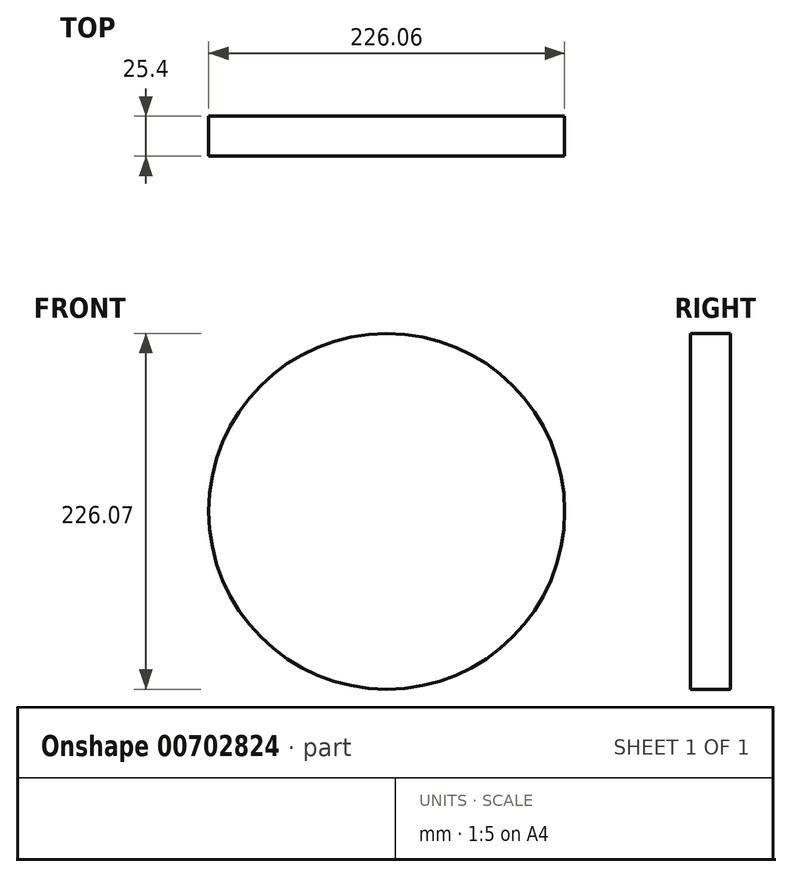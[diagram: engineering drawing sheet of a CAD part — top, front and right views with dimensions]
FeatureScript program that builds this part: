
annotation { "Feature Type Name" : "Feature", "Feature Type Description" : "" }
export const myFeature = defineFeature(function(context is Context, id is Id, definition is map)
    precondition{}
    {
        {
            var Q0;
            Q0=qCreatedBy(makeId("Front.planeOp"),FACE);
            var sketch = newSketch(context, id + "F0", { "sketchPlane" : qUnion([Q0])});
            skCircle(sketch, "E0", {"center": v(-64.91, 32.9) * mm, "radius": 113.03 * mm});
            skSolve(sketch);
        }
        {
            var Q0;
            Q0=qSketchRegion(id+"F0",true);
            extrude(context, id + "F1", {"entities" : qUnion([Q0]), "depth" : 25.4 * mm, "offsetDistance" : 25.4 * mm});
        }
    });
